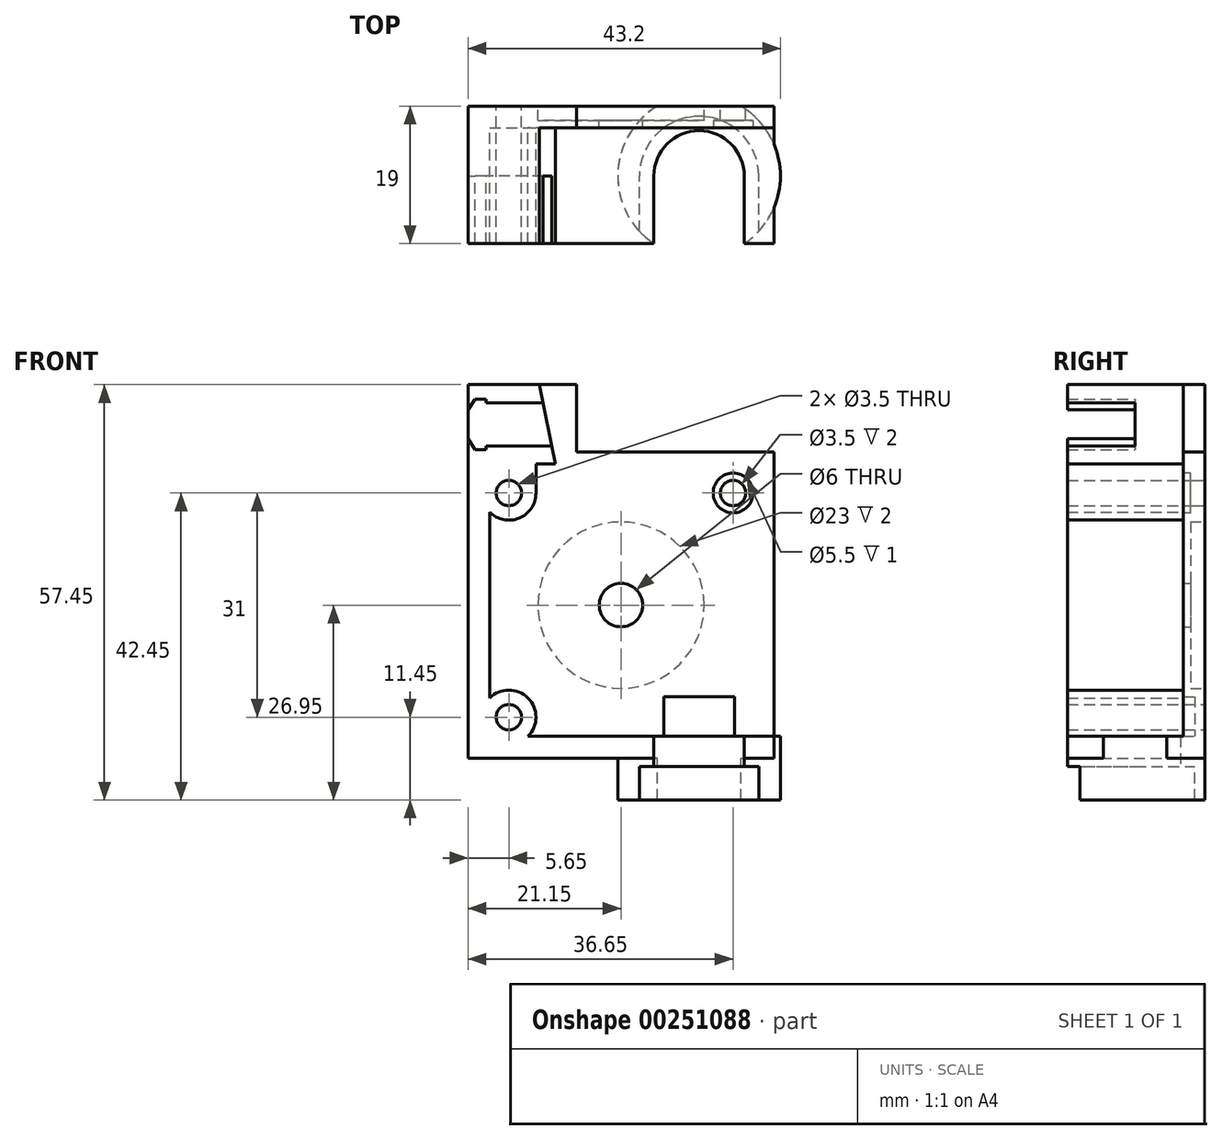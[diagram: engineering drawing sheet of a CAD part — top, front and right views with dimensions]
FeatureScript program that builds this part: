
annotation { "Feature Type Name" : "Feature", "Feature Type Description" : "" }
export const myFeature = defineFeature(function(context is Context, id is Id, definition is map)
    precondition{}
    {
        {
            var Q0;
            Q0=qCreatedBy(makeId("Front.planeOp"),FACE);
            var sketch = newSketch(context, id + "F0", { "sketchPlane" : qUnion([Q0])});
            skLineSegment(sketch, "E0.bottom", {"start": v(21.15, 21.15) * mm, "end": v(-21.15, 21.15) * mm});
            skLineSegment(sketch, "E0.top", {"start": v(21.15, -21.15) * mm, "end": v(-21.15, -21.15) * mm});
            skLineSegment(sketch, "E0.left", {"start": v(21.15, 21.15) * mm, "end": v(21.15, -21.15) * mm});
            skLineSegment(sketch, "E0.right", {"start": v(-21.15, 21.15) * mm, "end": v(-21.15, -21.15) * mm});
            skPoint(sketch, "E0.middle", {"position": v(0, 0) * mm});
            skCircle(sketch, "E1", {"center": v(-15.5, 15.5) * mm, "radius": 1.75 * mm});
            skCircle(sketch, "E2.MirrorC", {"center": v(15.5, 15.5) * mm, "radius": 1.75 * mm});
            skCircle(sketch, "E3.MirrorC", {"center": v(-15.5, -15.5) * mm, "radius": 1.75 * mm});
            skCircle(sketch, "E4.MirrorC", {"center": v(15.5, -15.5) * mm, "radius": 1.75 * mm, "construction": true});
            skCircle(sketch, "E5", {"center": v(0, 0) * mm, "radius": 3 * mm});
            skSolve(sketch);
        }
        {
            var Q0;
            Q0 = qSketchRegion(id + "F0", true);
            extrude(context, id + "F1", {"entities" : qUnion([Q0]), "depth" : 3 * mm});
        }
        {
            var Q0;
            Q0=makeQuery(id+"F1.opExtrude","CAP_FACE",FACE,{"disambiguationData":[OSD([sQuery(id+"F0.wireOp",EDGE,"E0.bottom"),sQuery(id+"F0.wireOp",EDGE,"E0.top"),sQuery(id+"F0.wireOp",EDGE,"E0.left"),sQuery(id+"F0.wireOp",EDGE,"E0.right"),sQuery(id+"F0.wireOp",EDGE,"E1"),sQuery(id+"F0.wireOp",EDGE,"E2.MirrorC"),sQuery(id+"F0.wireOp",EDGE,"E3.MirrorC"),sQuery(id+"F0.wireOp",EDGE,"E4.MirrorC"),sQuery(id+"F0.wireOp",EDGE,"E5")])],"isStart":true});
            var sketch = newSketch(context, id + "F2", { "sketchPlane" : qUnion([Q0])});
            skCircle(sketch, "E6", {"center": v(0, 0) * mm, "radius": 11.5 * mm});
            skSolve(sketch);
        }
        {
            var Q0;
            Q0 = qSketchRegion(id + "F2", true);
            extrude(context, id + "F3", {"entities" : qUnion([Q0]), "operationType" : NewBodyOperationType.REMOVE, "oppositeDirection" : true, "depth" : 2 * mm});
        }
        {
            var Q0;
            Q0=makeQuery(id+"F1.opExtrude","CAP_FACE",FACE,{"disambiguationData":[OSD([sQuery(id+"F0.wireOp",EDGE,"E0.bottom"),sQuery(id+"F0.wireOp",EDGE,"E0.top"),sQuery(id+"F0.wireOp",EDGE,"E0.left"),sQuery(id+"F0.wireOp",EDGE,"E0.right"),sQuery(id+"F0.wireOp",EDGE,"E1"),sQuery(id+"F0.wireOp",EDGE,"E2.MirrorC"),sQuery(id+"F0.wireOp",EDGE,"E3.MirrorC"),sQuery(id+"F0.wireOp",EDGE,"E4.MirrorC"),sQuery(id+"F0.wireOp",EDGE,"E5")])],"isStart":false});
            var sketch = newSketch(context, id + "F4", { "sketchPlane" : qUnion([Q0])});
            skLineSegment(sketch, "E7", {"start": v(-21.15, 21.15) * mm, "end": v(-11.75, 21.15) * mm});
            skLineSegment(sketch, "E8.MirrorCS", {"start": v(-11.75, 15.5) * mm, "end": v(-11.75, 21.15) * mm});
            skCircle(sketch, "E9.0", {"center": v(-15.5, 15.5) * mm, "radius": 1.75 * mm});
            skCircle(sketch, "E9.1", {"center": v(15.5, 15.5) * mm, "radius": 1.75 * mm});
            skCircle(sketch, "E9.3", {"center": v(-15.5, -15.5) * mm, "radius": 1.75 * mm});
            skArc(sketch, "E10", {"start": v(-18.15, 12.85) * mm, "mid": v(-14.06, 12.04) * mm, "end": v(-11.75, 15.5) * mm});
            skArc(sketch, "E11.MirrorC", {"start": v(-18.15, -12.85) * mm, "mid": v(-12.85, -12.85) * mm, "end": v(-12.85, -18.15) * mm});
            skLineSegment(sketch, "E12.0", {"start": v(21.15, -21.15) * mm, "end": v(-21.15, -21.15) * mm});
            skLineSegment(sketch, "E13.trimOffspring", {"start": v(-18.15, 12.85) * mm, "end": v(-18.15, -12.85) * mm});
            skLineSegment(sketch, "E14.trimOffspring", {"start": v(21.15, -18.15) * mm, "end": v(-12.85, -18.15) * mm});
            skLineSegment(sketch, "E15", {"start": v(21.15, -18.15) * mm, "end": v(21.15, -21.15) * mm});
            skLineSegment(sketch, "E16.trimOffspring", {"start": v(-21.15, 21.15) * mm, "end": v(-21.15, -21.15) * mm});
            skLineSegment(sketch, "E17", {"start": v(-11.75, 15.5) * mm, "end": v(-11.75, 15.5) * mm});
            skSolve(sketch);
        }
        {
            var Q0;
            Q0=makeQuery(id+"F4.imprint","IMPRINT",FACE,{"disambiguationData":[TD([[makeQuery(id+"F4.imprint","IMPRINT",EDGE,{"derivedFrom":sQuery(id+"F4.wireOp",EDGE,"E7")}),1.0]])]});
            extrude(context, id + "F5", {"entities" : qUnion([Q0]), "operationType" : NewBodyOperationType.ADD, "depth" : 16 * mm});
        }
        {
            var Q0;
            Q0=qCreatedBy(makeId("Front.planeOp"),FACE);
            cPlane(context, id + "F6", {"entities" : qUnion([Q0]), "cplaneType" : CPlaneType.OFFSET, "offset" : (7.65 + 2) * mm, "width" : 150 * mm, "height" : 150 * mm});
        }
        {
            var Q0;
            Q0=qCreatedBy(id+"F6.planeOp",FACE);
            var sketch = newSketch(context, id + "F7", { "sketchPlane" : qUnion([Q0])});
            skCircle(sketch, "E18", {"center": v(0, 0) * mm, "radius": 6 * mm, "construction": true});
            skCircle(sketch, "E19", {"center": v(15.5, 15.5) * mm, "radius": 15.92 * mm, "construction": true});
            skCircle(sketch, "E20", {"center": v(15.5, 15.5) * mm, "radius": 4.5 * mm, "construction": true});
            skCircle(sketch, "E21", {"center": v(15.5, 15.5) * mm, "radius": 3.75 * mm, "construction": true});
            skLineSegment(sketch, "E22.1", {"start": v(10.8, 32.66) * mm, "end": v(10.8, -28.23) * mm, "construction": true});
            skSolve(sketch);
        }
        {
            var Q0;
            Q0=qCreatedBy(id+"F6.planeOp",FACE);
            var sketch = newSketch(context, id + "F8", { "sketchPlane" : qUnion([Q0])});
            skLineSegment(sketch, "E23", {"start": v(-29.91, 25) * mm, "end": v(26.14, 25) * mm, "construction": true});
            skLineSegment(sketch, "E24", {"start": v(0, 28) * mm, "end": v(-18.65, 28) * mm});
            skLineSegment(sketch, "E25.MirrorCS", {"start": v(0, 22) * mm, "end": v(-18.65, 22) * mm});
            skLineSegment(sketch, "E26.left", {"start": v(-18.65, 28.5) * mm, "end": v(-18.65, 28) * mm});
            skLineSegment(sketch, "E27.trimOffspring", {"start": v(-18.65, 28.5) * mm, "end": v(-20.15, 28.5) * mm});
            skLineSegment(sketch, "E28.MirrorCS", {"start": v(-18.65, 21.5) * mm, "end": v(-18.65, 22) * mm});
            skLineSegment(sketch, "E29.trimOffspring", {"start": v(-18.65, 21.5) * mm, "end": v(-20.15, 21.5) * mm});
            skLineSegment(sketch, "E30", {"start": v(-21.15, 27) * mm, "end": v(-21.15, 23) * mm});
            skLineSegment(sketch, "E31", {"start": v(0, 28) * mm, "end": v(0, 22) * mm});
            skLineSegment(sketch, "E32", {"start": v(-21.15, 27) * mm, "end": v(-20.15, 28.5) * mm});
            skLineSegment(sketch, "E33.MirrorCS", {"start": v(-21.15, 23) * mm, "end": v(-20.15, 21.5) * mm});
            skSolve(sketch);
        }
        {
            var Q0;
            Q0=qCreatedBy(makeId("Front.planeOp"),FACE);
            var sketch = newSketch(context, id + "F9", { "sketchPlane" : qUnion([Q0])});
            skLineSegment(sketch, "E34.left", {"start": v(-21.15, 19.5) * mm, "end": v(-21.15, 30.5) * mm});
            skLineSegment(sketch, "E34.right", {"start": v(-6.15, 19.5) * mm, "end": v(-6.15, 30.5) * mm});
            skLineSegment(sketch, "E35.MirrorCS", {"start": v(-21.15, 30.5) * mm, "end": v(-6.15, 30.5) * mm});
            skCircle(sketch, "E36.0", {"center": v(-15.5, 15.5) * mm, "radius": 1.75 * mm});
            skLineSegment(sketch, "E37.trimOffspring", {"start": v(-21.15, 19.5) * mm, "end": v(-6.15, 19.5) * mm});
            skSolve(sketch);
        }
        {
            var Q0;
            {var subQ0=sQuery(id+"F9.wireOp",EDGE,"E34.top");Q0=makeQuery(id+"F9.imprint","IMPRINT",FACE,{"disambiguationData":[TD([[makeQuery(id+"F9.imprint","IMPRINT",EDGE,{"derivedFrom":subQ0}),-1.0]])]});}
            var Q1;
            Q1=makeQuery(id+"F9.imprint","IMPRINT",FACE,{"disambiguationData":[TD([[makeQuery(id+"F9.imprint","IMPRINT",EDGE,{"derivedFrom":sQuery(id+"F9.wireOp",EDGE,"E34.left")}),-1.0]])]});
            var Q2;
            Q2=makeQuery(id+"F5.opExtrude","CAP_FACE",FACE,{"disambiguationData":[OSD([sQuery(id+"F4.wireOp",EDGE,"E7"),sQuery(id+"F4.wireOp",EDGE,"E8.MirrorCS"),sQuery(id+"F4.wireOp",EDGE,"E9.0"),sQuery(id+"F4.wireOp",EDGE,"E9.3"),sQuery(id+"F4.wireOp",EDGE,"E10"),sQuery(id+"F4.wireOp",EDGE,"E11.MirrorC"),sQuery(id+"F4.wireOp",EDGE,"E12.0"),sQuery(id+"F4.wireOp",EDGE,"E13.trimOffspring"),sQuery(id+"F4.wireOp",EDGE,"E14.trimOffspring"),sQuery(id+"F4.wireOp",EDGE,"E15"),sQuery(id+"F4.wireOp",EDGE,"E16.trimOffspring")])],"isStart":false});
            extrude(context, id + "F10", {"entities" : qUnion([Q0, Q1]), "operationType" : NewBodyOperationType.ADD, "endBound" : BoundingType.UP_TO_SURFACE, "endBoundEntityFace" : qUnion([Q2]), "depth" : 25 * mm});
        }
        {
            var Q0;
            Q0 = qSketchRegion(id + "F8", true);
            extrude(context, id + "F11", {"entities" : qUnion([Q0]), "operationType" : NewBodyOperationType.REMOVE, "depth" : 10 * mm});
        }
        {
            var Q0;
            Q0=qCreatedBy(id+"F6.planeOp",FACE);
            var sketch = newSketch(context, id + "F12", { "sketchPlane" : qUnion([Q0])});
            skLineSegment(sketch, "E38.0", {"start": v(10.8, 32.15) * mm, "end": v(10.8, -42.47) * mm, "construction": true});
            skLineSegment(sketch, "E39.bottom", {"start": v(19.05, -18.15) * mm, "end": v(17.05, -18.15) * mm, "construction": true});
            skLineSegment(sketch, "E39.top", {"start": v(19.05, -12.65) * mm, "end": v(2.55, -12.65) * mm, "construction": true});
            skLineSegment(sketch, "E39.left", {"start": v(19.05, -18.15) * mm, "end": v(19.05, -12.65) * mm, "construction": true});
            skLineSegment(sketch, "E39.right", {"start": v(2.55, -18.15) * mm, "end": v(2.55, -12.65) * mm, "construction": true});
            skPoint(sketch, "E39.middle", {"position": v(10.8, -15.4) * mm});
            skLineSegment(sketch, "E40.top", {"start": v(17.05, -22.35) * mm, "end": v(4.55, -22.35) * mm, "construction": true});
            skLineSegment(sketch, "E40.left", {"start": v(17.05, -18.15) * mm, "end": v(17.05, -22.35) * mm, "construction": true});
            skLineSegment(sketch, "E40.right", {"start": v(4.55, -18.15) * mm, "end": v(4.55, -22.35) * mm, "construction": true});
            skPoint(sketch, "E40.middle", {"position": v(10.8, -20.25) * mm});
            skLineSegment(sketch, "E41.bottom", {"start": v(19.05, -22.35) * mm, "end": v(17.05, -22.35) * mm, "construction": true});
            skLineSegment(sketch, "E41.top", {"start": v(19.05, -26.95) * mm, "end": v(2.55, -26.95) * mm, "construction": true});
            skLineSegment(sketch, "E41.left", {"start": v(19.05, -22.35) * mm, "end": v(19.05, -26.95) * mm, "construction": true});
            skLineSegment(sketch, "E41.right", {"start": v(2.55, -22.35) * mm, "end": v(2.55, -26.95) * mm, "construction": true});
            skPoint(sketch, "E41.middle", {"position": v(10.8, -24.65) * mm});
            skLineSegment(sketch, "E42.trimOffspring", {"start": v(4.55, -18.15) * mm, "end": v(2.55, -18.15) * mm, "construction": true});
            skLineSegment(sketch, "E43.trimOffspring", {"start": v(4.55, -22.35) * mm, "end": v(2.55, -22.35) * mm, "construction": true});
            skPoint(sketch, "E44", {"position": v(10.8, -5.16) * mm});
            skSolve(sketch);
        }
        {
            var Q0;
            Q0=qCreatedBy(id+"F6.planeOp",FACE);
            var sketch = newSketch(context, id + "F13", { "sketchPlane" : qUnion([Q0])});
            skLineSegment(sketch, "E45.0", {"start": v(19.05, -18.15) * mm, "end": v(19.05, -12.65) * mm});
            skLineSegment(sketch, "E45.1", {"start": v(19.05, -18.15) * mm, "end": v(17.05, -18.15) * mm});
            skLineSegment(sketch, "E45.2", {"start": v(17.05, -18.15) * mm, "end": v(17.05, -22.35) * mm});
            skLineSegment(sketch, "E45.3", {"start": v(19.05, -22.35) * mm, "end": v(17.05, -22.35) * mm});
            skLineSegment(sketch, "E45.4", {"start": v(19.05, -22.35) * mm, "end": v(19.05, -26.95) * mm});
            skLineSegment(sketch, "E46", {"start": v(19.05, -12.65) * mm, "end": v(10.8, -12.65) * mm});
            skLineSegment(sketch, "E47", {"start": v(10.8, -12.65) * mm, "end": v(10.8, -26.95) * mm});
            skLineSegment(sketch, "E48", {"start": v(10.8, -26.95) * mm, "end": v(19.05, -26.95) * mm});
            skSolve(sketch);
        }
        {
            var Q0;
            Q0 = qSketchRegion(id + "F13", true);
            var Q1;
            Q1=sQuery(id+"F12.wireOp",EDGE,"E38.0");
            revolve(context, id + "F14", {"operationType" : NewBodyOperationType.REMOVE, "entities" : qUnion([Q0]), "axis" : qUnion([Q1]), "revolveType" : RevolveType.FULL, "oppositeDirection" : true});
        }
        {
            var Q0;
            Q0=qCreatedBy(id+"F6.planeOp",FACE);
            var sketch = newSketch(context, id + "F15", { "sketchPlane" : qUnion([Q0])});
            skLineSegment(sketch, "E49", {"start": v(8.3, 45.28) * mm, "end": v(8.3, -57.7) * mm, "construction": true});
            skLineSegment(sketch, "E50", {"start": v(13.3, -58.45) * mm, "end": v(13.3, 44.53) * mm, "construction": true});
            skLineSegment(sketch, "E51", {"start": v(8.3, -6.21) * mm, "end": v(13.3, -6.21) * mm, "construction": true});
            skPoint(sketch, "E52", {"position": v(10.8, -6.21) * mm});
            skLineSegment(sketch, "E53.0", {"start": v(2.55, -18.15) * mm, "end": v(2.55, -12.65) * mm, "construction": true});
            skLineSegment(sketch, "E53.1", {"start": v(4.55, -18.15) * mm, "end": v(2.55, -18.15) * mm, "construction": true});
            skLineSegment(sketch, "E53.2", {"start": v(4.55, -18.15) * mm, "end": v(4.55, -22.35) * mm, "construction": true});
            skLineSegment(sketch, "E53.3", {"start": v(4.55, -22.35) * mm, "end": v(2.55, -22.35) * mm, "construction": true});
            skLineSegment(sketch, "E53.4", {"start": v(2.55, -22.35) * mm, "end": v(2.55, -26.95) * mm, "construction": true});
            skLineSegment(sketch, "E53.5", {"start": v(17.05, -18.15) * mm, "end": v(17.05, -22.35) * mm});
            skLineSegment(sketch, "E53.6", {"start": v(19.05, -22.35) * mm, "end": v(17.05, -22.35) * mm});
            skLineSegment(sketch, "E53.7", {"start": v(19.05, -18.15) * mm, "end": v(17.05, -18.15) * mm});
            skLineSegment(sketch, "E53.8", {"start": v(19.05, -18.15) * mm, "end": v(19.05, -18.15) * mm});
            skLineSegment(sketch, "E53.9", {"start": v(19.05, -22.35) * mm, "end": v(19.05, -26.95) * mm});
            skLineSegment(sketch, "E53.10", {"start": v(19.05, -26.95) * mm, "end": v(2.55, -26.95) * mm, "construction": true});
            skLineSegment(sketch, "E54.0", {"start": v(22.05, -18.15) * mm, "end": v(22.05, -26.95) * mm});
            skLineSegment(sketch, "E54.1", {"start": v(22.05, -29.95) * mm, "end": v(-0.45, -29.95) * mm, "construction": true});
            skLineSegment(sketch, "E54.2", {"start": v(-0.45, -21.15) * mm, "end": v(-0.45, -29.95) * mm, "construction": true});
            skLineSegment(sketch, "E55", {"start": v(19.05, -18.15) * mm, "end": v(22.05, -18.15) * mm});
            skLineSegment(sketch, "E56", {"start": v(19.05, -26.95) * mm, "end": v(22.05, -26.95) * mm});
            skLineSegment(sketch, "E57", {"start": v(22.05, -26.95) * mm, "end": v(22.05, -29.95) * mm, "construction": true});
            skSolve(sketch);
        }
        {
            var Q0;
            Q0 = qSketchRegion(id + "F15", true);
            var Q1;
            Q1=sQuery(id+"F15.wireOp",EDGE,"E53.2");
            var Q2;
            Q2=sQuery(id+"F15.wireOp",EDGE,"E53.0");
            var Q3;
            Q3=sQuery(id+"F15.wireOp",EDGE,"E54.2");
            var Q4;
            Q4=sQuery(id+"F15.wireOp",EDGE,"E53.3");
            var Q5;
            Q5=sQuery(id+"F15.wireOp",EDGE,"E53.4");
            var Q6;
            Q6=sQuery(id+"F15.wireOp",EDGE,"E53.1");
            var Q7;
            Q7=sQuery(id+"F12.wireOp",EDGE,"E38.0");
            revolve(context, id + "F16", {"operationType" : NewBodyOperationType.ADD, "entities" : qUnion([Q0]), "surfaceEntities" : qUnion([Q1, Q2, Q3, Q4, Q5, Q6]), "axis" : qUnion([Q7]), "revolveType" : RevolveType.FULL});
        }
        {
            var Q0;
            Q0=qCreatedBy(id+"F6.planeOp",FACE);
            var sketch = newSketch(context, id + "F17", { "sketchPlane" : qUnion([Q0])});
            skLineSegment(sketch, "E58.0", {"start": v(2.55, -18.15) * mm, "end": v(2.55, -12.65) * mm});
            skLineSegment(sketch, "E58.1", {"start": v(19.05, -12.65) * mm, "end": v(2.55, -12.65) * mm});
            skLineSegment(sketch, "E58.2", {"start": v(19.05, -18.15) * mm, "end": v(19.05, -12.65) * mm});
            skLineSegment(sketch, "E58.3", {"start": v(17.05, -18.15) * mm, "end": v(17.05, -22.35) * mm});
            skLineSegment(sketch, "E58.4", {"start": v(4.55, -18.15) * mm, "end": v(4.55, -22.35) * mm});
            skLineSegment(sketch, "E58.5", {"start": v(4.55, -18.15) * mm, "end": v(2.55, -18.15) * mm});
            skLineSegment(sketch, "E58.6", {"start": v(19.05, -18.15) * mm, "end": v(17.05, -18.15) * mm});
            skLineSegment(sketch, "E58.7", {"start": v(19.05, -22.35) * mm, "end": v(17.05, -22.35) * mm});
            skLineSegment(sketch, "E58.8", {"start": v(19.05, -22.35) * mm, "end": v(19.05, -26.95) * mm});
            skLineSegment(sketch, "E58.9", {"start": v(4.55, -22.35) * mm, "end": v(2.55, -22.35) * mm});
            skLineSegment(sketch, "E58.10", {"start": v(2.55, -22.35) * mm, "end": v(2.55, -26.95) * mm});
            skLineSegment(sketch, "E58.11", {"start": v(19.05, -26.95) * mm, "end": v(2.55, -26.95) * mm});
            skSolve(sketch);
        }
        {
            var Q0;
            Q0 = qSketchRegion(id + "F17", true);
            extrude(context, id + "F18", {"entities" : qUnion([Q0]), "operationType" : NewBodyOperationType.REMOVE, "endBound" : BoundingType.THROUGH_ALL, "depth" : 25 * mm});
        }
        {
            var Q0;
            Q0=qCreatedBy(makeId("Right.planeOp"),FACE);
            var sketch = newSketch(context, id + "F19", { "sketchPlane" : qUnion([Q0])});
            skLineSegment(sketch, "E59.bottom", {"start": v(0, 47.05) * mm, "end": v(28.32, 47.05) * mm});
            skLineSegment(sketch, "E59.top", {"start": v(0, -52.65) * mm, "end": v(28.32, -52.65) * mm});
            skLineSegment(sketch, "E59.left", {"start": v(0, 47.05) * mm, "end": v(0, -52.65) * mm});
            skLineSegment(sketch, "E59.right", {"start": v(28.32, 47.05) * mm, "end": v(28.32, -52.65) * mm});
            skSolve(sketch);
        }
        {
            var Q0;
            Q0=makeQuery(id+"F19.imprint","IMPRINT",FACE,{"disambiguationData":[TD([[makeQuery(id+"F19.imprint","IMPRINT",EDGE,{"derivedFrom":sQuery(id+"F19.wireOp",EDGE,"E59.bottom")}),-1.0]])]});
            extrude(context, id + "F20", {"entities" : qUnion([Q0]), "operationType" : NewBodyOperationType.REMOVE, "endBound" : BoundingType.THROUGH_ALL, "depth" : 25 * mm});
        }
        {
            var Q0;
            Q0=makeQuery(id+"F1.opExtrude","CAP_FACE",FACE,{"disambiguationData":[OSD([sQuery(id+"F0.wireOp",EDGE,"E0.bottom"),sQuery(id+"F0.wireOp",EDGE,"E0.top"),sQuery(id+"F0.wireOp",EDGE,"E0.left"),sQuery(id+"F0.wireOp",EDGE,"E0.right"),sQuery(id+"F0.wireOp",EDGE,"E1"),sQuery(id+"F0.wireOp",EDGE,"E2.MirrorC"),sQuery(id+"F0.wireOp",EDGE,"E3.MirrorC"),sQuery(id+"F0.wireOp",EDGE,"E5")])],"isStart":false});
            var sketch = newSketch(context, id + "F21", { "sketchPlane" : qUnion([Q0])});
            skArc(sketch, "E60", {"start": v(4.9, 1) * mm, "mid": v(1, -4.9) * mm, "end": v(-4.9, -1) * mm});
            skLineSegment(sketch, "E61", {"start": v(4.9, 1) * mm, "end": v(-4.02, 45.1) * mm});
            skLineSegment(sketch, "E62", {"start": v(-4.9, -1) * mm, "end": v(-13.82, 43.12) * mm});
            skArc(sketch, "E63", {"start": v(-13.82, 43.12) * mm, "mid": v(-9.91, 49) * mm, "end": v(-4.02, 45.1) * mm});
            skCircle(sketch, "E64", {"center": v(-0.23, 16.28) * mm, "radius": 8 * mm, "construction": true});
            skLineSegment(sketch, "E65", {"start": v(-8.92, 44.1) * mm, "end": v(0, 0) * mm, "construction": true});
            skCircle(sketch, "E66.0", {"center": v(15.5, 15.5) * mm, "radius": 3.75 * mm, "construction": true});
            skLineSegment(sketch, "E67", {"start": v(-0.23, 16.28) * mm, "end": v(-3.17, 15.68) * mm, "construction": true});
            skSolve(sketch);
        }
        {
            var Q0;
            Q0 = qSketchRegion(id + "F21", true);
            extrude(context, id + "F22", {"entities" : qUnion([Q0]), "operationType" : NewBodyOperationType.REMOVE, "endBound" : BoundingType.THROUGH_ALL, "depth" : 25 * mm});
        }
        {
            var Q0;
            Q0=makeQuery(id+"F22.boolean.opBoolean","MERGE",FACE,{"derivedFrom":[makeQuery(id+"F1.opExtrude","CAP_FACE",FACE,{"disambiguationData":[OSD([sQuery(id+"F0.wireOp",EDGE,"E0.bottom"),sQuery(id+"F0.wireOp",EDGE,"E0.top"),sQuery(id+"F0.wireOp",EDGE,"E0.left"),sQuery(id+"F0.wireOp",EDGE,"E0.right"),sQuery(id+"F0.wireOp",EDGE,"E1"),sQuery(id+"F0.wireOp",EDGE,"E2.MirrorC"),sQuery(id+"F0.wireOp",EDGE,"E3.MirrorC"),sQuery(id+"F0.wireOp",EDGE,"E5")])],"isStart":false}),makeQuery(id+"F22.opExtrude","CAP_FACE",FACE,{"disambiguationData":[OSD([sQuery(id+"F21.wireOp",EDGE,"E60"),sQuery(id+"F21.wireOp",EDGE,"E61"),sQuery(id+"F21.wireOp",EDGE,"E62"),sQuery(id+"F21.wireOp",EDGE,"E63")])],"isStart":true})]});
            var sketch = newSketch(context, id + "F23", { "sketchPlane" : qUnion([Q0])});
            skCircle(sketch, "E68", {"center": v(15.5, 15.5) * mm, "radius": 2.75 * mm});
            skSolve(sketch);
        }
        {
            var Q0;
            Q0=makeQuery(id+"F23.imprint","IMPRINT",FACE,{"disambiguationData":[TD([[makeQuery(id+"F23.imprint","IMPRINT",EDGE,{"derivedFrom":sQuery(id+"F23.wireOp",EDGE,"E68")}),1.0]])]});
            extrude(context, id + "F24", {"entities" : qUnion([Q0]), "operationType" : NewBodyOperationType.REMOVE, "oppositeDirection" : true, "depth" : 1 * mm});
        }
    });
